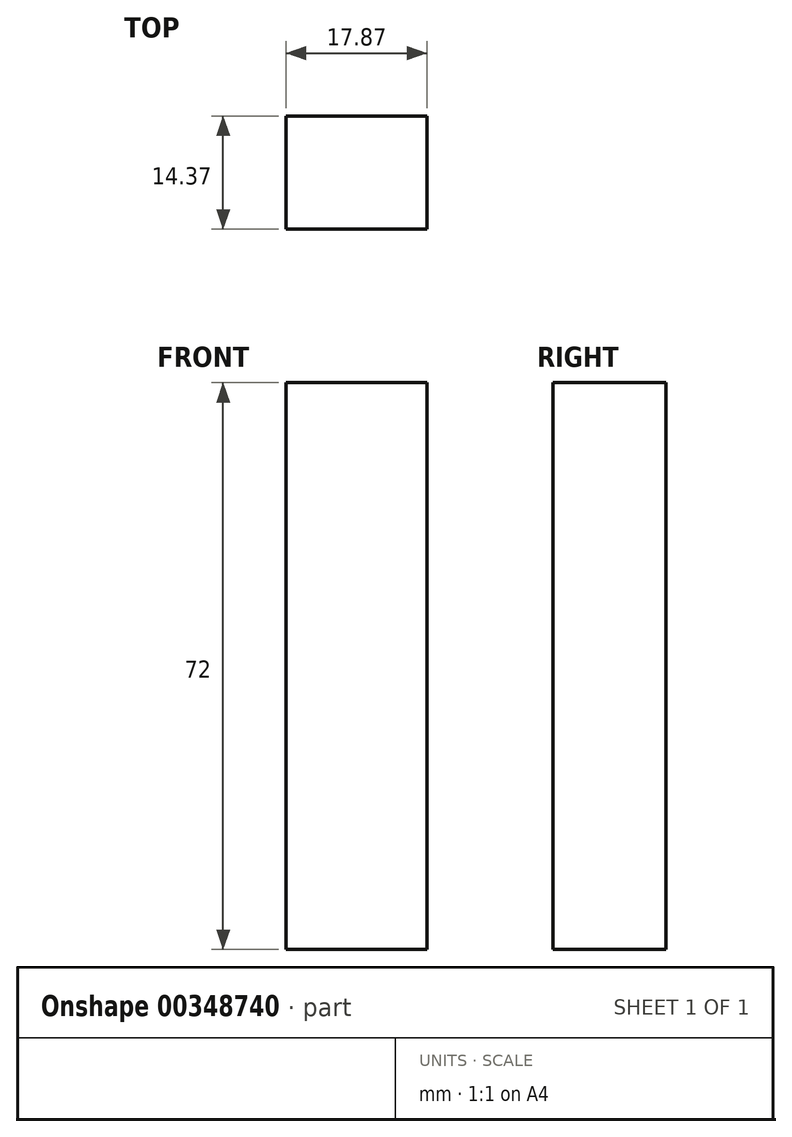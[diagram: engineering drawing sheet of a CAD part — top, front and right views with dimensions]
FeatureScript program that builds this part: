
annotation { "Feature Type Name" : "Feature", "Feature Type Description" : "" }
export const myFeature = defineFeature(function(context is Context, id is Id, definition is map)
    precondition{}
    {
        {
            var Q0;
            Q0=qCreatedBy(makeId("Top.planeOp"),FACE);
            var sketch = newSketch(context, id + "F0", { "sketchPlane" : qUnion([Q0])});
            skLineSegment(sketch, "E0.bottom", {"start": v(-66.24, -61.35) * mm, "end": v(-48.37, -61.35) * mm});
            skLineSegment(sketch, "E0.top", {"start": v(-66.24, -75.72) * mm, "end": v(-48.37, -75.72) * mm});
            skLineSegment(sketch, "E0.left", {"start": v(-66.24, -61.35) * mm, "end": v(-66.24, -75.72) * mm});
            skLineSegment(sketch, "E0.right", {"start": v(-48.37, -61.35) * mm, "end": v(-48.37, -75.72) * mm});
            skSolve(sketch);
        }
        {
            var Q0;
            Q0 = qSketchRegion(id + "F0", true);
            extrude(context, id + "F1", {"entities" : qUnion([Q0]), "depth" : 72 * mm});
        }
    });
